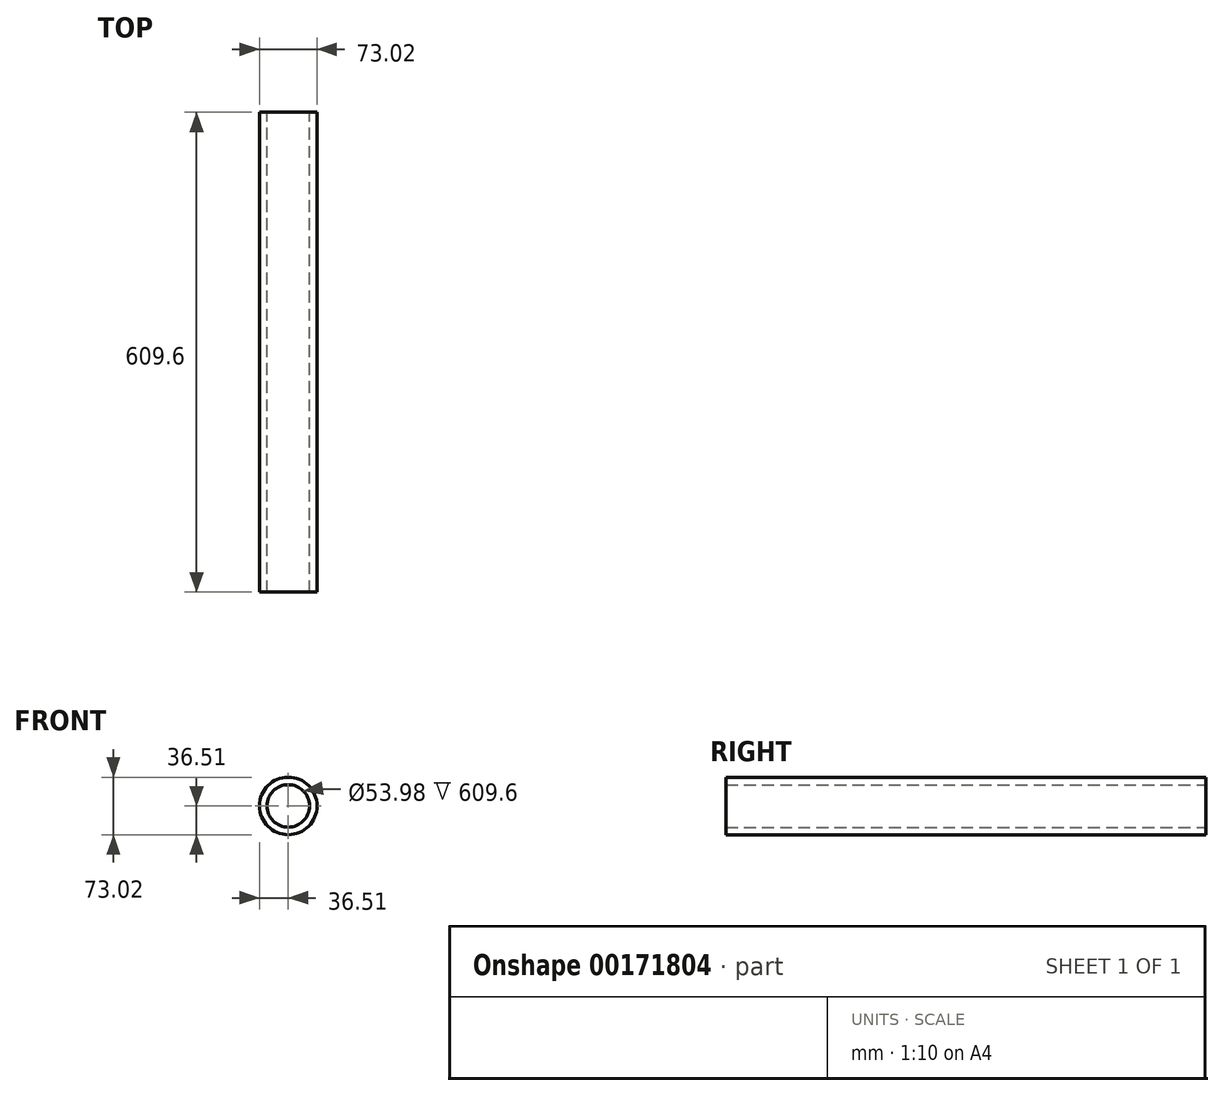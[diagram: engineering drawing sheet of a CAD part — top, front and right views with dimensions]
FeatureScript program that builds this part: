
annotation { "Feature Type Name" : "Feature", "Feature Type Description" : "" }
export const myFeature = defineFeature(function(context is Context, id is Id, definition is map)
    precondition{}
    {
        {
            var Q0;
            Q0=qCreatedBy(makeId("Front.planeOp"),FACE);
            var sketch = newSketch(context, id + "F0", { "sketchPlane" : qUnion([Q0])});
            skCircle(sketch, "E0", {"center": v(0, 0) * mm, "radius": 36.51 * mm});
            skCircle(sketch, "E1", {"center": v(0, 0) * mm, "radius": 26.99 * mm});
            skSolve(sketch);
        }
        {
            var Q0;
            Q0=makeQuery(id+"F0.imprint","IMPRINT",FACE,{"disambiguationData":[TD([[makeQuery(id+"F0.imprint","IMPRINT",EDGE,{"derivedFrom":sQuery(id+"F0.wireOp",EDGE,"E0")}),1.0]])]});
            extrude(context, id + "F1", {"entities" : qUnion([Q0]), "endBound" : BoundingType.SYMMETRIC, "depth" : 609.6 * mm});
        }
    });
